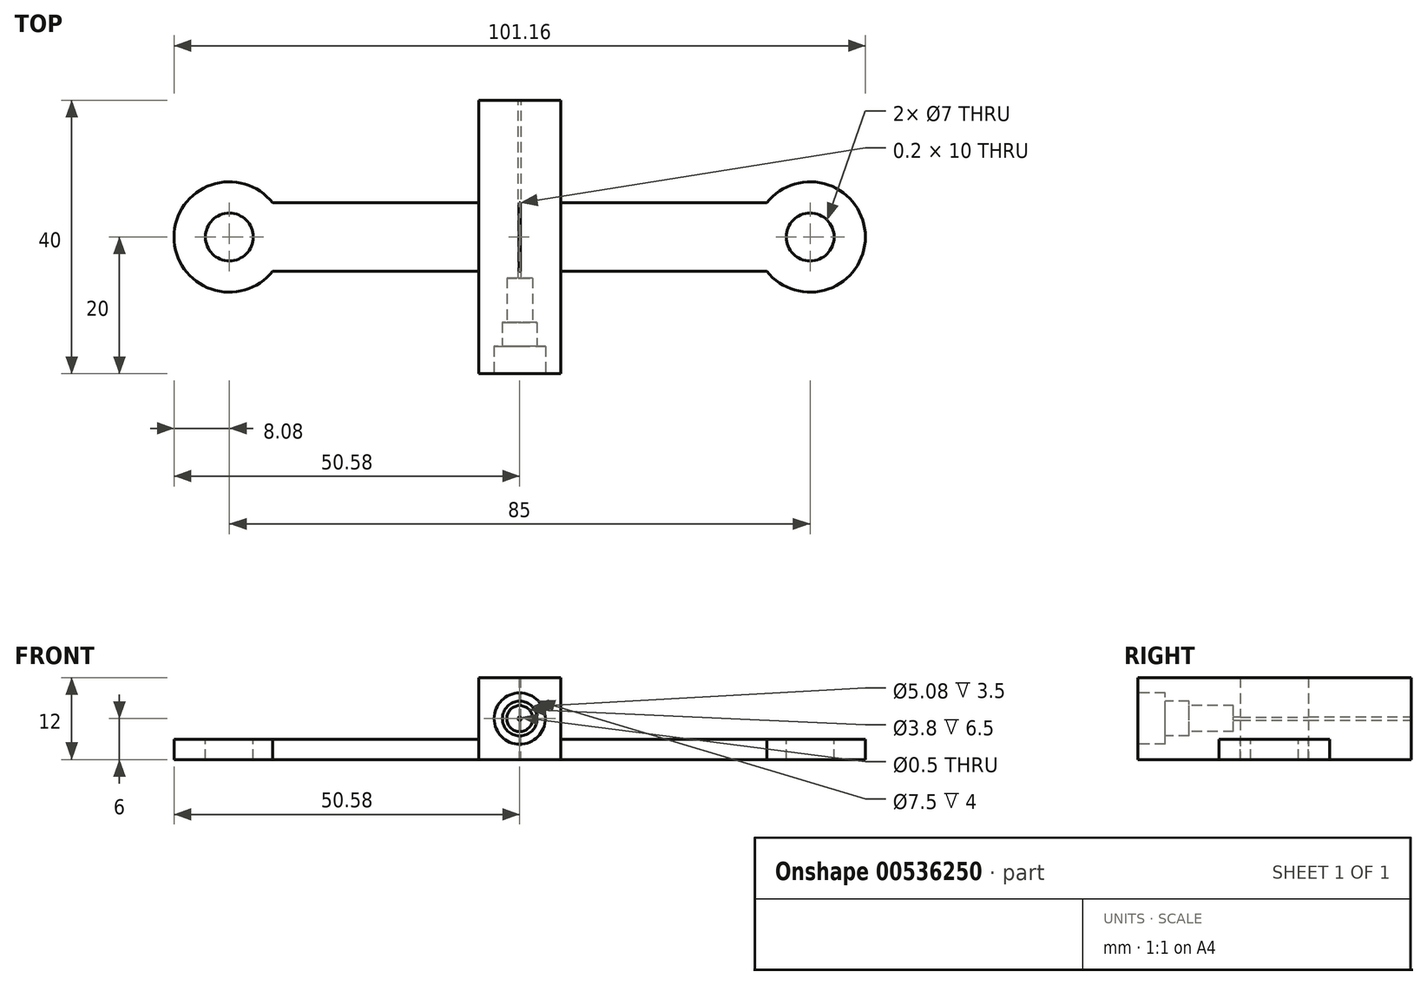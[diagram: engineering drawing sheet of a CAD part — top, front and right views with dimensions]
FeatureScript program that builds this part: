
annotation { "Feature Type Name" : "Feature", "Feature Type Description" : "" }
export const myFeature = defineFeature(function(context is Context, id is Id, definition is map)
    precondition{}
    {
        {
            var Q0;
            Q0=qCreatedBy(makeId("Top.planeOp"),FACE);
            var sketch = newSketch(context, id + "F0", { "sketchPlane" : qUnion([Q0])});
            skLineSegment(sketch, "E0.bottom", {"start": v(42.5, -5) * mm, "end": v(-42.5, -5) * mm});
            skLineSegment(sketch, "E0.top", {"start": v(42.5, 5) * mm, "end": v(-42.5, 5) * mm});
            skLineSegment(sketch, "E0.left", {"start": v(42.5, -5) * mm, "end": v(42.5, 5) * mm});
            skLineSegment(sketch, "E0.right", {"start": v(-42.5, -5) * mm, "end": v(-42.5, 5) * mm});
            skPoint(sketch, "E0.middle", {"position": v(0, 0) * mm});
            skCircle(sketch, "E1", {"center": v(-42.5, 0) * mm, "radius": 8.08 * mm});
            skCircle(sketch, "E2.MirrorC", {"center": v(42.5, 0) * mm, "radius": 8.08 * mm});
            skSolve(sketch);
        }
        {
            var Q0;
            {var subQ0=sQuery(id+"F0.wireOp",EDGE,"E0.left");Q0=makeQuery(id+"F0.imprint","IMPRINT",FACE,{"disambiguationData":[TD([[makeQuery(id+"F0.imprint","IMPRINT",EDGE,{"derivedFrom":subQ0}),-1.0]])]});}
            var Q1;
            {var subQ0=sQuery(id+"F0.wireOp",EDGE,"E0.right");Q1=makeQuery(id+"F0.imprint","IMPRINT",FACE,{"disambiguationData":[TD([[makeQuery(id+"F0.imprint","IMPRINT",EDGE,{"derivedFrom":subQ0}),1.0]])]});}
            var Q2;
            {var subQ0=sQuery(id+"F0.wireOp",EDGE,"E0.left");Q2=makeQuery(id+"F0.imprint","IMPRINT",FACE,{"disambiguationData":[TD([[makeQuery(id+"F0.imprint","IMPRINT",EDGE,{"derivedFrom":subQ0}),1.0]])]});}
            var Q3;
            {var subQ0=sQuery(id+"F0.wireOp",EDGE,"E2.MirrorC");var subQ1=sQuery(id+"F0.wireOp",EDGE,"E0.bottom");var subQ2=makeQuery(id+"F0.imprint","INTERSECT",VERTEX,{"derivedFrom":[subQ1,subQ0]});Q3=makeQuery(id+"F0.imprint","IMPRINT",FACE,{"disambiguationData":[TD([[makeQuery(id+"F0.imprint","IMPRINT",EDGE,{"disambiguationData":[TD([[subQ2,-1.0]])],"derivedFrom":subQ1}),-1.0]])]});}
            var Q4;
            {var subQ0=sQuery(id+"F0.wireOp",EDGE,"E0.right");Q4=makeQuery(id+"F0.imprint","IMPRINT",FACE,{"disambiguationData":[TD([[makeQuery(id+"F0.imprint","IMPRINT",EDGE,{"derivedFrom":subQ0}),-1.0]])]});}
            extrude(context, id + "F1", {"entities" : qUnion([Q0, Q1, Q2, Q3, Q4]), "depth" : 3 * mm, "offsetDistance" : 25 * mm});
        }
        {
            var Q0;
            Q0=makeQuery(id+"F1.opExtrude","CAP_FACE",FACE,{"disambiguationData":[OSD([sQuery(id+"F0.wireOp",EDGE,"E0.bottom"),sQuery(id+"F0.wireOp",EDGE,"E0.top"),sQuery(id+"F0.wireOp",EDGE,"E1"),sQuery(id+"F0.wireOp",EDGE,"E2.MirrorC")])],"isStart":false});
            var sketch = newSketch(context, id + "F2", { "sketchPlane" : qUnion([Q0])});
            skCircle(sketch, "E3", {"center": v(-42.5, 0) * mm, "radius": 3.05 * mm});
            skCircle(sketch, "E4.MirrorC", {"center": v(42.5, 0) * mm, "radius": 3.05 * mm});
            skSolve(sketch);
        }
        {
            var Q0;
            Q0=sQuery(id+"F2.wireOp",VERTEX,"E3.center");
            var Q1;
            Q1=sQuery(id+"F2.wireOp",VERTEX,"E4.MirrorC.center");
            var Q2;
            Q2=makeQuery(id+"F1.opExtrude","SWEPT_BODY",BODY,{"disambiguationData":[OSD([sQuery(id+"F0.wireOp",EDGE,"E0.bottom"),sQuery(id+"F0.wireOp",EDGE,"E0.top"),sQuery(id+"F0.wireOp",EDGE,"E1"),sQuery(id+"F0.wireOp",EDGE,"E2.MirrorC")])]});
            hole(context, id + "F3", {"style" : HoleStyle.SIMPLE, "endStyle" : HoleEndStyle.THROUGH, "holeDiameter" : 7 * mm, "isTappedThrough" : true, "tappedDepth" : 12 * mm, "tapClearance" : 3, "locations" : qUnion([Q0, Q1]), "scope" : qUnion([Q2])});
        }
        {
            var Q0;
            Q0=qCreatedBy(makeId("Front.planeOp"),FACE);
            var sketch = newSketch(context, id + "F4", { "sketchPlane" : qUnion([Q0])});
            skCircle(sketch, "E5", {"center": v(0, 21.1) * mm, "radius": 0.2 * mm});
            skSolve(sketch);
        }
        {
            var Q0;
            Q0=qSketchRegion(id+"F4",true);
            extrude(context, id + "F5", {"entities" : qUnion([Q0]), "operationType" : NewBodyOperationType.REMOVE, "endBound" : BoundingType.SYMMETRIC, "oppositeDirection" : true, "depth" : 25 * mm, "offsetDistance" : 25 * mm});
        }
        {
            var Q0;
            Q0=qCreatedBy(makeId("Top.planeOp"),FACE);
            var sketch = newSketch(context, id + "F6", { "sketchPlane" : qUnion([Q0])});
            skLineSegment(sketch, "E6.bottom", {"start": v(6, 20) * mm, "end": v(-6, 20) * mm});
            skLineSegment(sketch, "E6.top", {"start": v(6, -20) * mm, "end": v(-6, -20) * mm});
            skLineSegment(sketch, "E6.left", {"start": v(6, 20) * mm, "end": v(6, -20) * mm});
            skLineSegment(sketch, "E6.right", {"start": v(-6, 20) * mm, "end": v(-6, -20) * mm});
            skPoint(sketch, "E6.middle", {"position": v(0, 0) * mm});
            skSolve(sketch);
        }
        {
            var Q0;
            Q0 = qSketchRegion(id + "F6", true);
            extrude(context, id + "F7", {"entities" : qUnion([Q0]), "operationType" : NewBodyOperationType.ADD, "depth" : 12 * mm, "offsetDistance" : 25 * mm});
        }
        {
            var Q0;
            Q0=qCreatedBy(makeId("Top.planeOp"),FACE);
            var sketch = newSketch(context, id + "F8", { "sketchPlane" : qUnion([Q0])});
            skLineSegment(sketch, "E7.bottom", {"start": v(-0.1, 5) * mm, "end": v(0.1, 5) * mm});
            skLineSegment(sketch, "E7.top", {"start": v(-0.1, -5) * mm, "end": v(0.1, -5) * mm});
            skLineSegment(sketch, "E7.left", {"start": v(-0.1, 5) * mm, "end": v(-0.1, -5) * mm});
            skLineSegment(sketch, "E7.right", {"start": v(0.1, 5) * mm, "end": v(0.1, -5) * mm});
            skPoint(sketch, "E7.middle", {"position": v(0, 0) * mm});
            skSolve(sketch);
        }
        {
            var Q0;
            Q0 = qSketchRegion(id + "F8", true);
            extrude(context, id + "F9", {"entities" : qUnion([Q0]), "operationType" : NewBodyOperationType.REMOVE, "depth" : 12 * mm, "offsetDistance" : 25 * mm});
        }
        {
            var Q0;
            Q0=qCreatedBy(makeId("Front.planeOp"),FACE);
            var sketch = newSketch(context, id + "F10", { "sketchPlane" : qUnion([Q0])});
            skCircle(sketch, "E8", {"center": v(0, 6) * mm, "radius": 0.25 * mm});
            skSolve(sketch);
        }
        {
            var Q0;
            Q0 = qSketchRegion(id + "F10", true);
            var Q1;
            Q1=sQuery(id+"F10.wireOp",EDGE,"E8");
            extrude(context, id + "F11", {"entities" : qUnion([Q0]), "operationType" : NewBodyOperationType.REMOVE, "surfaceEntities" : qUnion([Q1]), "endBound" : BoundingType.SYMMETRIC, "depth" : 50 * mm, "offsetDistance" : 25 * mm});
        }
        {
            var Q0;
            Q0=makeQuery(id+"F7.opExtrude","SWEPT_FACE",FACE,{"disambiguationData":[OSD([sQuery(id+"F6.wireOp",EDGE,"E6.top")])]});
            var sketch = newSketch(context, id + "F12", { "sketchPlane" : qUnion([Q0])});
            skCircle(sketch, "E9", {"center": v(0, 6) * mm, "radius": 1.9 * mm});
            skSolve(sketch);
        }
        {
            var Q0;
            Q0 = qSketchRegion(id + "F12", true);
            extrude(context, id + "F13", {"entities" : qUnion([Q0]), "operationType" : NewBodyOperationType.REMOVE, "oppositeDirection" : true, "depth" : 14 * mm, "offsetDistance" : 25 * mm});
        }
        {
            var Q0;
            Q0=makeQuery(id+"F7.opExtrude","SWEPT_FACE",FACE,{"disambiguationData":[OSD([sQuery(id+"F6.wireOp",EDGE,"E6.top")])]});
            var sketch = newSketch(context, id + "F14", { "sketchPlane" : qUnion([Q0])});
            skCircle(sketch, "E10", {"center": v(0, 6) * mm, "radius": 2.54 * mm});
            skSolve(sketch);
        }
        {
            var Q0;
            Q0 = qSketchRegion(id + "F14", true);
            extrude(context, id + "F15", {"entities" : qUnion([Q0]), "operationType" : NewBodyOperationType.REMOVE, "oppositeDirection" : true, "depth" : 7.5 * mm, "offsetDistance" : 25 * mm});
        }
        {
            var Q0;
            Q0=makeQuery(id+"F7.opExtrude","SWEPT_FACE",FACE,{"disambiguationData":[OSD([sQuery(id+"F6.wireOp",EDGE,"E6.top")])]});
            var sketch = newSketch(context, id + "F16", { "sketchPlane" : qUnion([Q0])});
            skCircle(sketch, "E11", {"center": v(0, 6) * mm, "radius": 3.75 * mm});
            skSolve(sketch);
        }
        {
            var Q0;
            Q0 = qSketchRegion(id + "F16", true);
            extrude(context, id + "F17", {"entities" : qUnion([Q0]), "operationType" : NewBodyOperationType.REMOVE, "oppositeDirection" : true, "depth" : 4 * mm, "offsetDistance" : 25 * mm});
        }
    });
